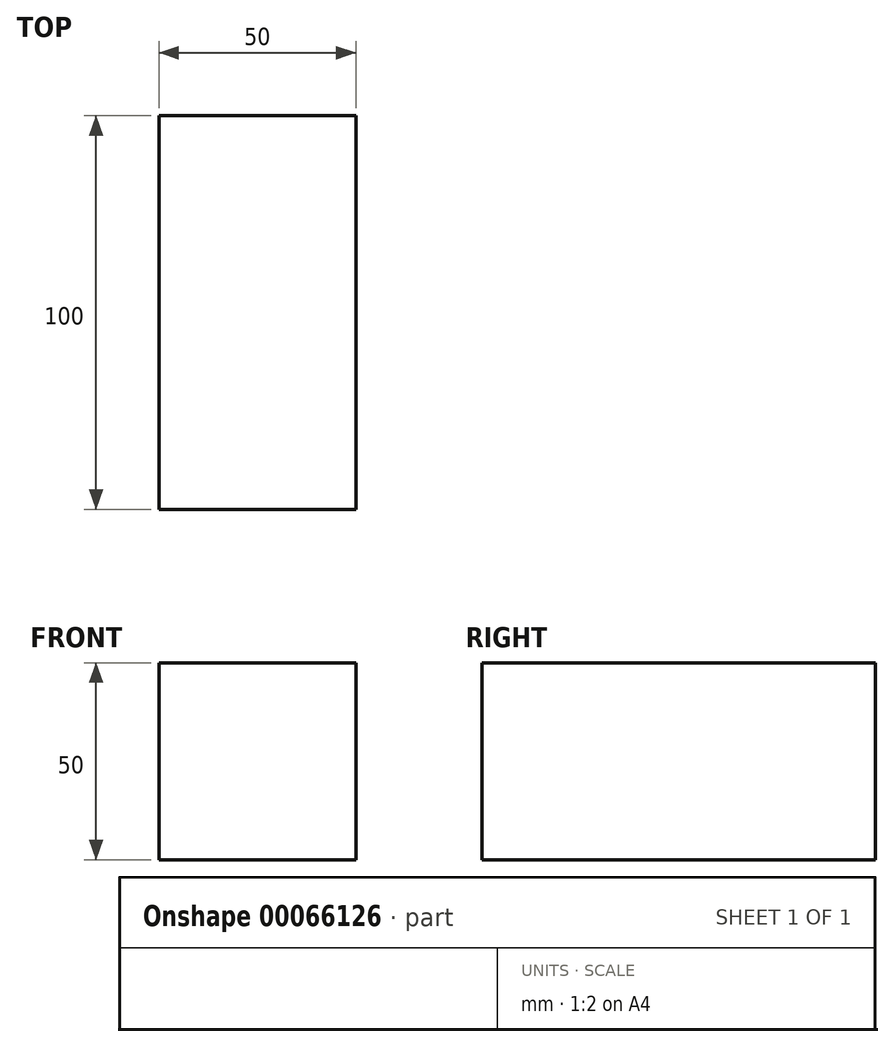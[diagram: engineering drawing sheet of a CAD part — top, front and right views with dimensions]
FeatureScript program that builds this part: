
annotation { "Feature Type Name" : "Feature", "Feature Type Description" : "" }
export const myFeature = defineFeature(function(context is Context, id is Id, definition is map)
    precondition{}
    {
        {
            var Q0;
            Q0=qCreatedBy(makeId("Front.planeOp"),FACE);
            var sketch = newSketch(context, id + "F0", { "sketchPlane" : qUnion([Q0])});
            skLineSegment(sketch, "E0.rect.bottom", {"start": v(-25, 25) * mm, "end": v(25, 25) * mm});
            skLineSegment(sketch, "E0.rect.top", {"start": v(-25, -25) * mm, "end": v(25, -25) * mm});
            skLineSegment(sketch, "E0.rect.left", {"start": v(-25, 25) * mm, "end": v(-25, -25) * mm});
            skLineSegment(sketch, "E0.rect.right", {"start": v(25, 25) * mm, "end": v(25, -25) * mm});
            skPoint(sketch, "E0.rect.middle", {"position": v(0, 0) * mm});
            skSolve(sketch);
        }
        {
            var Q0;
            Q0 = qSketchRegion(id + "F0", true);
            extrude(context, id + "F1", {"entities" : qUnion([Q0]), "depth" : 100 * mm});
        }
    });
